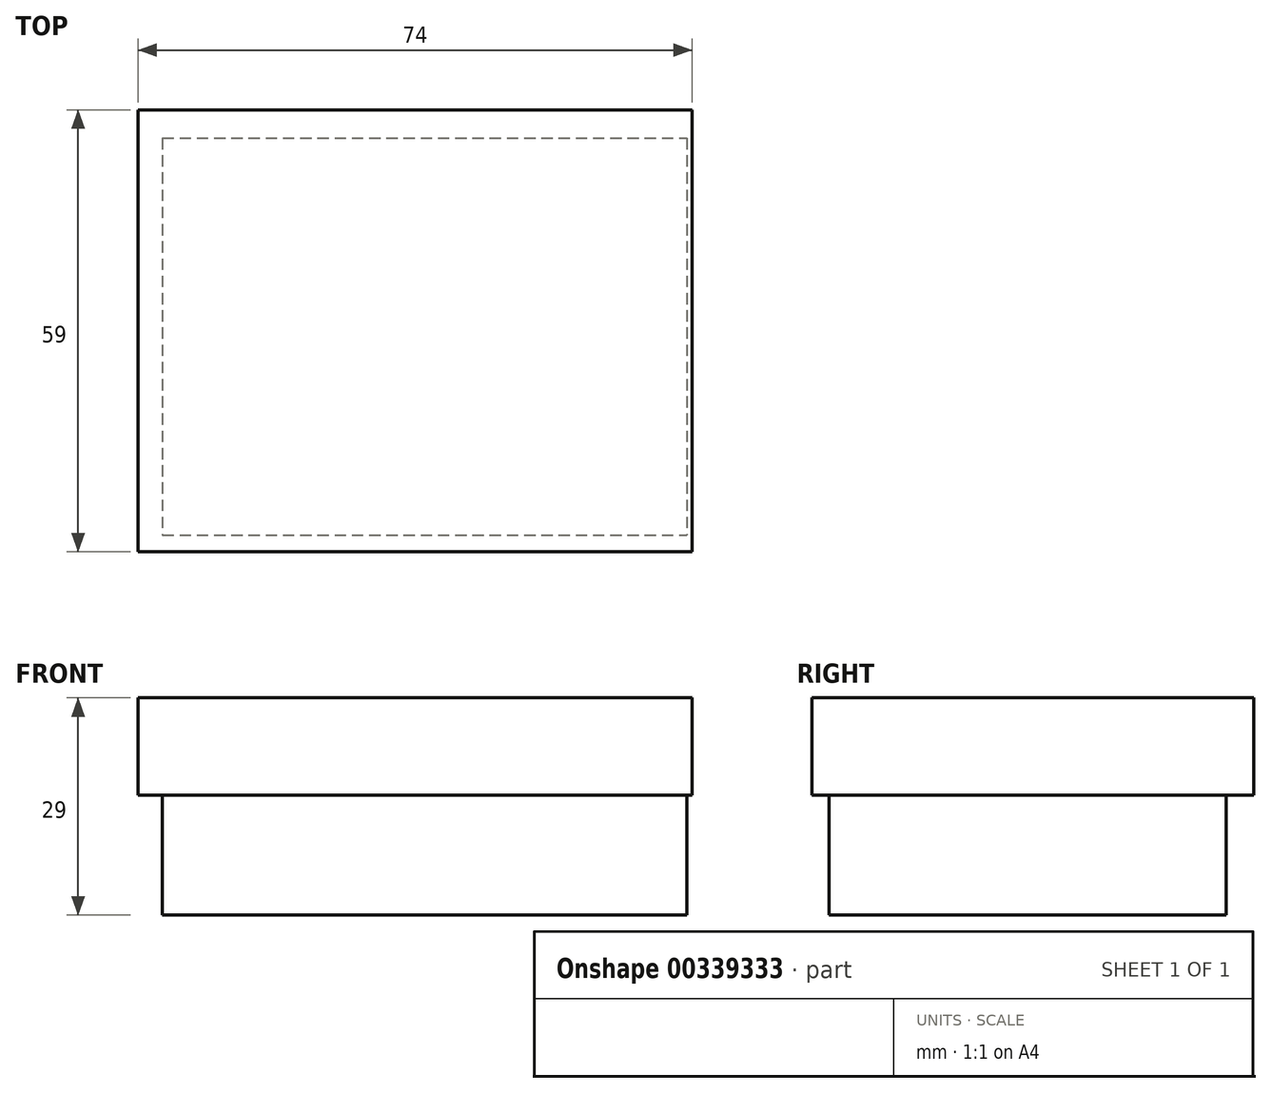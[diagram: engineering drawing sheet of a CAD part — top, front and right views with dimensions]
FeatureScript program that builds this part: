
annotation { "Feature Type Name" : "Feature", "Feature Type Description" : "" }
export const myFeature = defineFeature(function(context is Context, id is Id, definition is map)
    precondition{}
    {
        {
            var Q0;
            Q0=qCreatedBy(makeId("Top.planeOp"),FACE);
            var sketch = newSketch(context, id + "F0", { "sketchPlane" : qUnion([Q0])});
            skLineSegment(sketch, "E0.bottom", {"start": v(-123.12, 3.74) * mm, "end": v(-49.12, 3.74) * mm});
            skLineSegment(sketch, "E0.top", {"start": v(-123.12, -55.26) * mm, "end": v(-49.12, -55.26) * mm});
            skLineSegment(sketch, "E0.left", {"start": v(-123.12, 3.74) * mm, "end": v(-123.12, -55.26) * mm});
            skLineSegment(sketch, "E0.right", {"start": v(-49.12, 3.74) * mm, "end": v(-49.12, -55.26) * mm});
            skSolve(sketch);
        }
        {
            var Q0;
            Q0=makeQuery(id+"F0.imprint","IMPRINT",FACE,{"disambiguationData":[TD([[makeQuery(id+"F0.imprint","IMPRINT",EDGE,{"derivedFrom":sQuery(id+"F0.wireOp",EDGE,"E0.bottom")}),-1.0]])]});
            extrude(context, id + "F1", {"entities" : qUnion([Q0]), "depth" : 13 * mm});
        }
        {
            var Q0;
            Q0=qCreatedBy(makeId("Top.planeOp"),FACE);
            var sketch = newSketch(context, id + "F2", { "sketchPlane" : qUnion([Q0])});
            skLineSegment(sketch, "E1.bottom", {"start": v(-119.86, 0) * mm, "end": v(-49.86, 0) * mm});
            skLineSegment(sketch, "E1.top", {"start": v(-119.86, -53) * mm, "end": v(-49.86, -53) * mm});
            skLineSegment(sketch, "E1.left", {"start": v(-119.86, 0) * mm, "end": v(-119.86, -53) * mm});
            skLineSegment(sketch, "E1.right", {"start": v(-49.86, 0) * mm, "end": v(-49.86, -53) * mm});
            skSolve(sketch);
        }
        {
            var Q0;
            Q0 = qSketchRegion(id + "F2", true);
            extrude(context, id + "F3", {"entities" : qUnion([Q0]), "operationType" : NewBodyOperationType.ADD, "depth" : -3 * mm});
        }
        {
            var Q0;
            Q0=makeQuery(id+"F3.opExtrude","CAP_FACE",FACE,{"disambiguationData":[OSD([sQuery(id+"F2.wireOp",EDGE,"E1.bottom"),sQuery(id+"F2.wireOp",EDGE,"E1.top"),sQuery(id+"F2.wireOp",EDGE,"E1.left"),sQuery(id+"F2.wireOp",EDGE,"E1.right")])],"isStart":false});
            extrude(context, id + "F4", {"entities" : qUnion([Q0]), "operationType" : NewBodyOperationType.ADD, "depth" : 13 * mm});
        }
    });
